# Revit family: BIM_Model_Piranha_50_09_D_rfa
name_source: partatom
category: Mechanical Equipment
revit_build: Autodesk Revit 2018 (Build: 20170223_1515(x64)
units: mm (PartAtom-declared; Revit-internal decimal feet)

## family parameters
Always vertical = Yes
Cut with Voids When Loaded = No
Part Type = Normal
Room Calculation Point = No
Round Connector Dimension = Use Radius
Shared = No
Work Plane-Based = No

## types (2) — shared parameters
Cable Length (m) = As Per Specification
Capacity (m3/hr) = 30 m³
Description = Submersible pumps for problem-free pumping of sewage
containing faecal matter in pipe lines from 1¼” (DN 32).
Fasteners = Stainless steel 1.4401 (AISI 316)
Head (m) = 75 mm
Manufacturer = Sulzer
Model = Type ABS Piranha 09
Motor Housing = Cast Iron EN-GJL-250
Rotor Shaft = Stainless steel 1.4021 (AISI 420)
Speed (r/min) = 2900
Upper Lid = Stainless steel 1.4301 (AISI 304)
Volute = Cast Iron EN-GJL-250

## per-type parameters (varying)
| type | Cable Type (H07RN-F) | Impeller | Motor Power (kW) | Product Specification Link | Rated Current (A) | Rated Voltage (V) |
| PIRANHA_09_W | 3G1.0 | Polyamide | P1=2.56 P2=1.84 | ******** | 11.60 | 220-240 1~ |
| PIRANHA_09_D | 4G1.0 | Cast Iron EN-GJL-250 | P1=2.56 P2=2.00 | https://www.sulzer.com | 4.64 | 400 3~ |

## geometry (parser evidence)
native form markers: Sweep x3
no freeform markers — native parametric forms only
